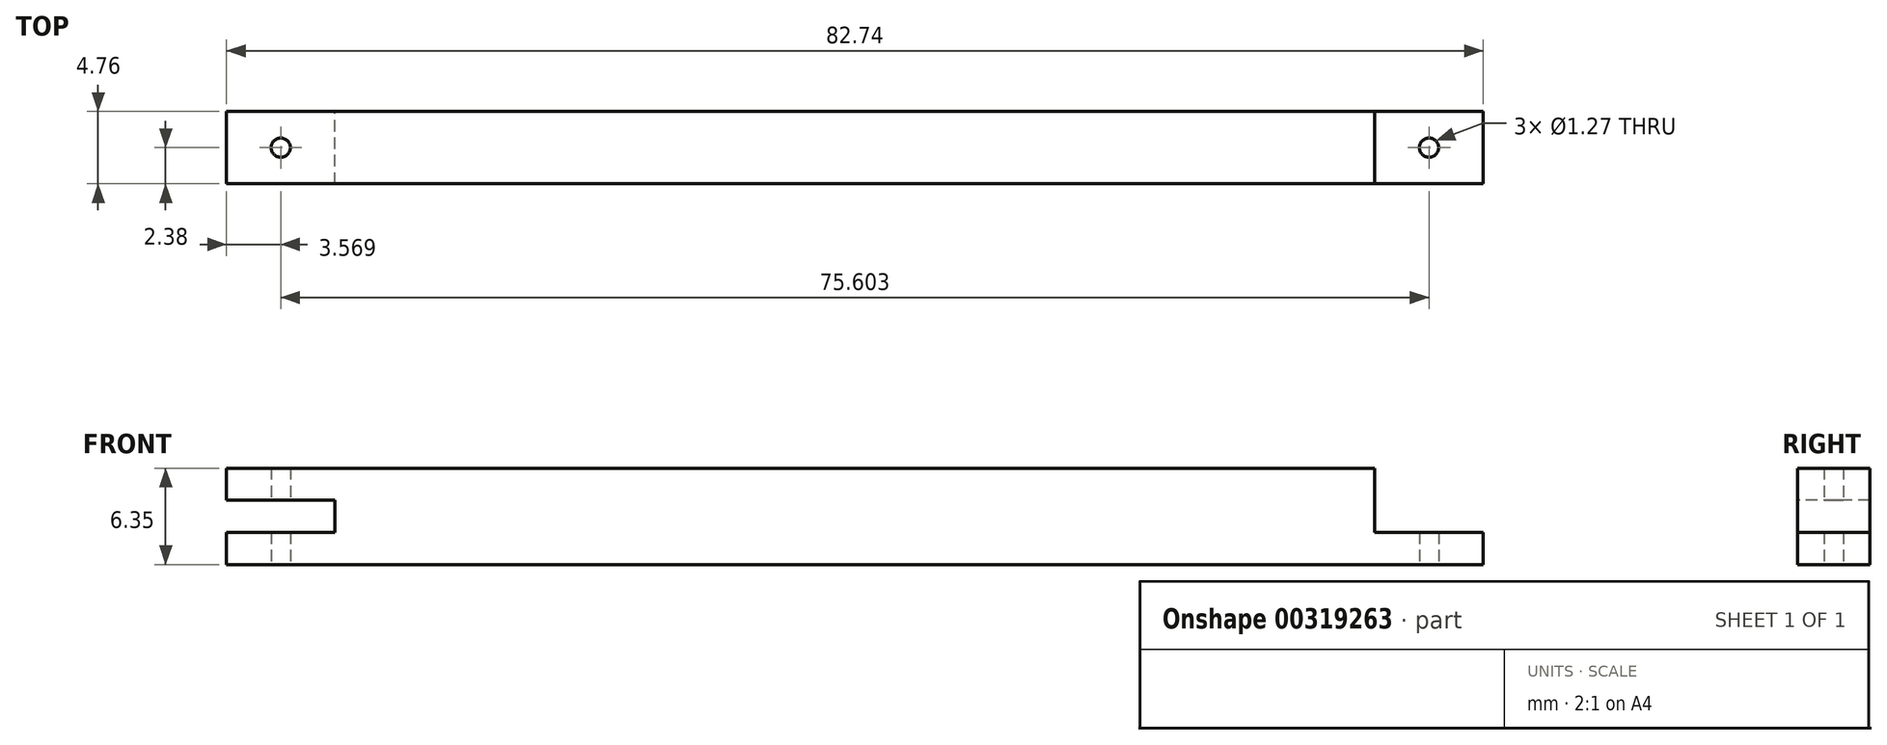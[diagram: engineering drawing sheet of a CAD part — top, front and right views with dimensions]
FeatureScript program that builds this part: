
annotation { "Feature Type Name" : "Feature", "Feature Type Description" : "" }
export const myFeature = defineFeature(function(context is Context, id is Id, definition is map)
    precondition{}
    {
        {
            var Q0;
            Q0=qCreatedBy(makeId("Top.planeOp"),FACE);
            var sketch = newSketch(context, id + "F0", { "sketchPlane" : qUnion([Q0])});
            skLineSegment(sketch, "E0.bottom", {"start": v(-41.37, 2.38) * mm, "end": v(41.37, 2.38) * mm});
            skLineSegment(sketch, "E0.top", {"start": v(-41.37, -2.38) * mm, "end": v(41.37, -2.38) * mm});
            skLineSegment(sketch, "E0.left", {"start": v(-41.37, 2.38) * mm, "end": v(-41.37, -2.38) * mm});
            skLineSegment(sketch, "E0.right", {"start": v(41.37, 2.38) * mm, "end": v(41.37, -2.38) * mm});
            skPoint(sketch, "E0.middle", {"position": v(0, 0) * mm});
            skLineSegment(sketch, "E1", {"start": v(0, 0) * mm, "end": v(-37.8, 0) * mm, "construction": true});
            skLineSegment(sketch, "E2", {"start": v(0, 0) * mm, "end": v(37.8, 0) * mm, "construction": true});
            skLineSegment(sketch, "E3", {"start": v(-37.8, 0) * mm, "end": v(-41.37, 0) * mm, "construction": true});
            skCircle(sketch, "E4", {"center": v(-37.8, 0) * mm, "radius": 0.64 * mm});
            skCircle(sketch, "E5", {"center": v(37.8, 0) * mm, "radius": 0.64 * mm});
            skLineSegment(sketch, "E6", {"start": v(-34.23, 2.38) * mm, "end": v(-34.23, -2.38) * mm});
            skLineSegment(sketch, "E7", {"start": v(34.23, 2.38) * mm, "end": v(34.23, -2.38) * mm});
            skSolve(sketch);
        }
        {
            var Q0;
            Q0 = qSketchRegion(id + "F0", true);
            extrude(context, id + "F1", {"entities" : qUnion([Q0]), "depth" : 2.12 * mm});
        }
        {
            var Q0;
            {var subQ0=sQuery(id+"F0.wireOp",EDGE,"E6");Q0=makeQuery(id+"F0.imprint","IMPRINT",FACE,{"disambiguationData":[TD([[makeQuery(id+"F0.imprint","IMPRINT",EDGE,{"derivedFrom":subQ0}),1.0]])]});}
            extrude(context, id + "F2", {"entities" : qUnion([Q0]), "operationType" : NewBodyOperationType.ADD, "depth" : 4.23 * mm});
        }
        {
            var Q0;
            {var subQ0=sQuery(id+"F0.wireOp",EDGE,"E0.left");Q0=makeQuery(id+"F0.imprint","IMPRINT",FACE,{"disambiguationData":[TD([[makeQuery(id+"F0.imprint","IMPRINT",EDGE,{"derivedFrom":subQ0}),1.0]])]});}
            var Q1;
            {var subQ0=sQuery(id+"F0.wireOp",EDGE,"E6");Q1=makeQuery(id+"F0.imprint","IMPRINT",FACE,{"disambiguationData":[TD([[makeQuery(id+"F0.imprint","IMPRINT",EDGE,{"derivedFrom":subQ0}),1.0]])]});}
            extrude(context, id + "F3", {"entities" : qUnion([Q0, Q1]), "operationType" : NewBodyOperationType.ADD, "depth" : 6.35 * mm, "hasSecondDirection" : true, "secondDirectionOppositeDirection" : false, "secondDirectionDepth" : 4.23 * mm});
        }
    });
